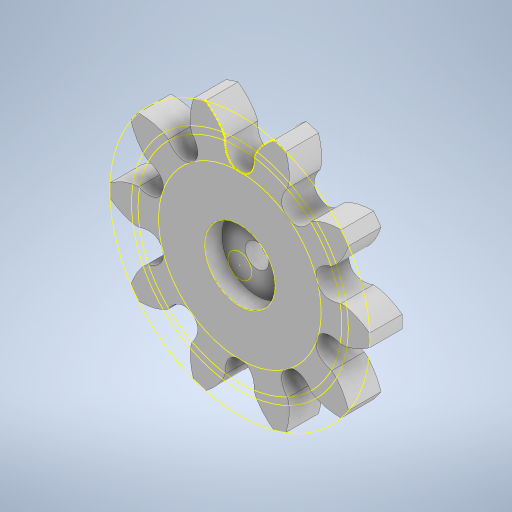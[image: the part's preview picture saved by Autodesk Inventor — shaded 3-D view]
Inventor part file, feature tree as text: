
AUTODESK INVENTOR PART (.ipt)
format: ipt  version: 2023 (Build 270158000, 158)  size: 410,112 bytes
history: native  units: mm
features: other x3, sketch x1
ambient origin geometry x8: Origin, YZ Plane, XZ Plane, XY Plane, X Axis, Y Axis, Z Axis, Center Point
bodies: Solid1 (feature_tree)
feature tree (4):
  other  "pinion_V6"
  other  "Solid1::pinion_V6"
  other  "TaggingFeature1"
  sketch  "Sketch1"  dims[d0=10.0mm]
